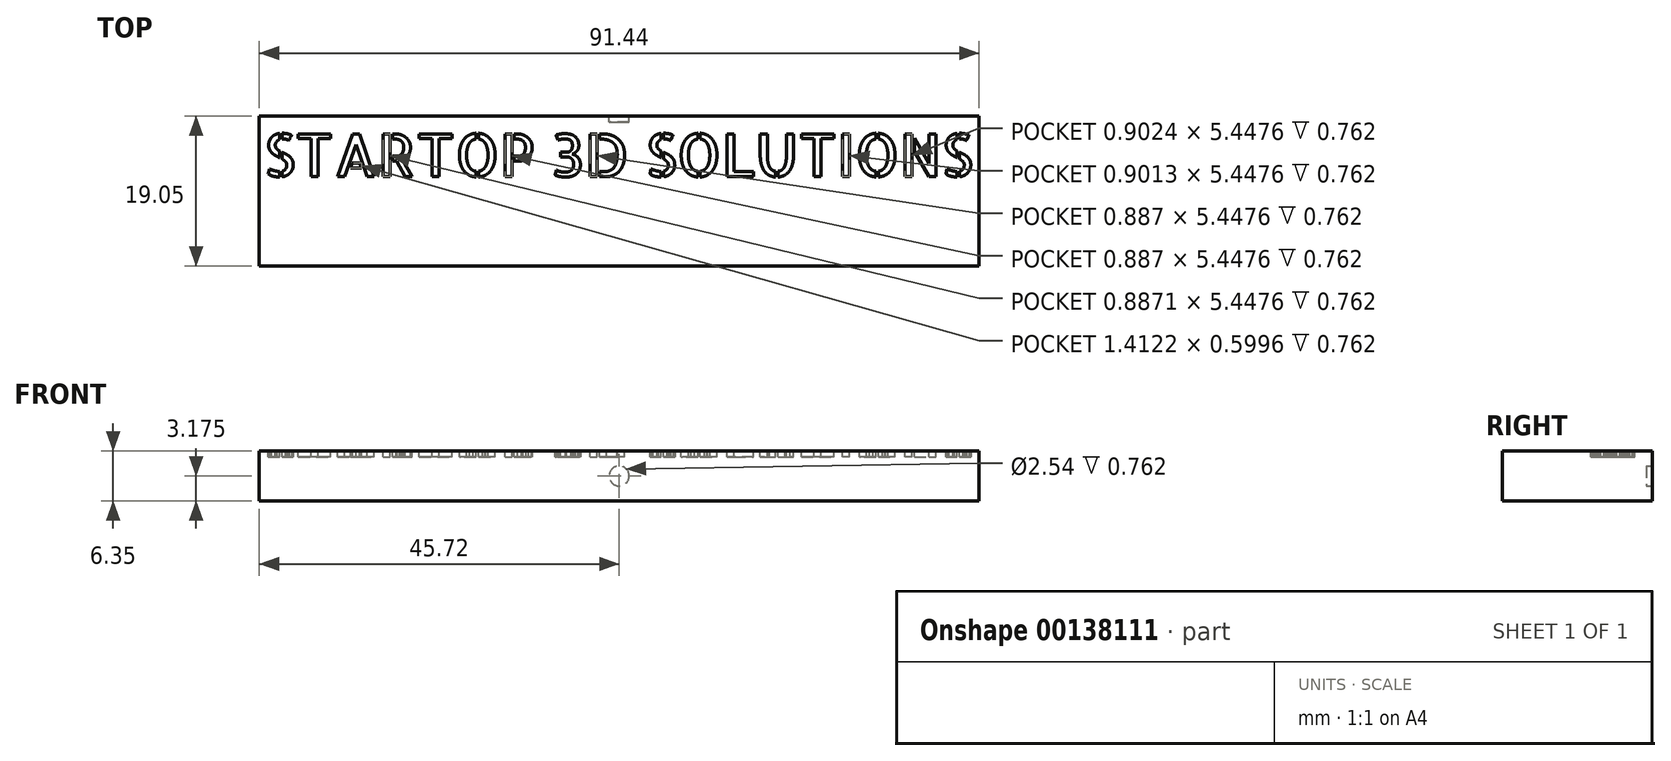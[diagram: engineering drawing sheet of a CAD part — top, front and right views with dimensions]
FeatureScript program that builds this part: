
annotation { "Feature Type Name" : "Feature", "Feature Type Description" : "" }
export const myFeature = defineFeature(function(context is Context, id is Id, definition is map)
    precondition{}
    {
        {
            var Q0;
            Q0=qCreatedBy(makeId("Top.planeOp"),FACE);
            var sketch = newSketch(context, id + "F0", { "sketchPlane" : qUnion([Q0])});
            skLineSegment(sketch, "E0.bottom", {"start": v(0, 0) * mm, "end": v(91.44, 0) * mm});
            skLineSegment(sketch, "E0.top", {"start": v(0, 19.05) * mm, "end": v(91.44, 19.05) * mm});
            skLineSegment(sketch, "E0.left", {"start": v(0, 0) * mm, "end": v(0, 19.05) * mm});
            skLineSegment(sketch, "E0.right", {"start": v(91.44, 0) * mm, "end": v(91.44, 19.05) * mm});
            skSolve(sketch);
        }
        {
            var Q0;
            Q0=qSketchRegion(id+"F0",true);
            extrude(context, id + "F1", {"entities" : qUnion([Q0]), "depth" : 6.35 * mm});
        }
        {
            var Q0;
            Q0=makeQuery(id+"F1.opExtrude","CAP_FACE",FACE,{"disambiguationData":[OSD([sQuery(id+"F0.wireOp",EDGE,"E0.bottom"),sQuery(id+"F0.wireOp",EDGE,"E0.top"),sQuery(id+"F0.wireOp",EDGE,"E0.left"),sQuery(id+"F0.wireOp",EDGE,"E0.right")])],"isStart":false});
            var sketch = newSketch(context, id + "F2", { "sketchPlane" : qUnion([Q0])});
            skLineSegment(sketch, "E1", {"start": v(0, 9.53) * mm, "end": v(91.44, 9.53) * mm, "construction": true});
            skText(sketch, "E2", { "text": "STARTOP 3D SOLUTIONS", "fontName": "AllertaStencil-Regular.ttf"});
            const initialGuessF2  = {"E2": [0.00056, 0.01133, 1, 0, 0.00545]};
            skSetInitialGuess(sketch, initialGuessF2);
            skSolve(sketch);
        }
        {
            var Q0;
            Q0=qSketchRegion(id+"F2",true);
            extrude(context, id + "F3", {"entities" : qUnion([Q0]), "operationType" : NewBodyOperationType.REMOVE, "oppositeDirection" : true, "depth" : 0.76 * mm});
        }
        {
            var Q0;
            Q0=makeQuery(id+"F1.opExtrude","SWEPT_FACE",FACE,{"disambiguationData":[OSD([sQuery(id+"F0.wireOp",EDGE,"E0.top")])]});
            var sketch = newSketch(context, id + "F4", { "sketchPlane" : qUnion([Q0])});
            skLineSegment(sketch, "E3", {"start": v(-91.44, 3.18) * mm, "end": v(0, 3.18) * mm, "construction": true});
            skCircle(sketch, "E4", {"center": v(-45.72, 3.18) * mm, "radius": 1.27 * mm});
            skSolve(sketch);
        }
        {
            var Q0;
            Q0 = qSketchRegion(id + "F4", true);
            extrude(context, id + "F5", {"entities" : qUnion([Q0]), "operationType" : NewBodyOperationType.REMOVE, "oppositeDirection" : true, "depth" : 0.76 * mm});
        }
    });
